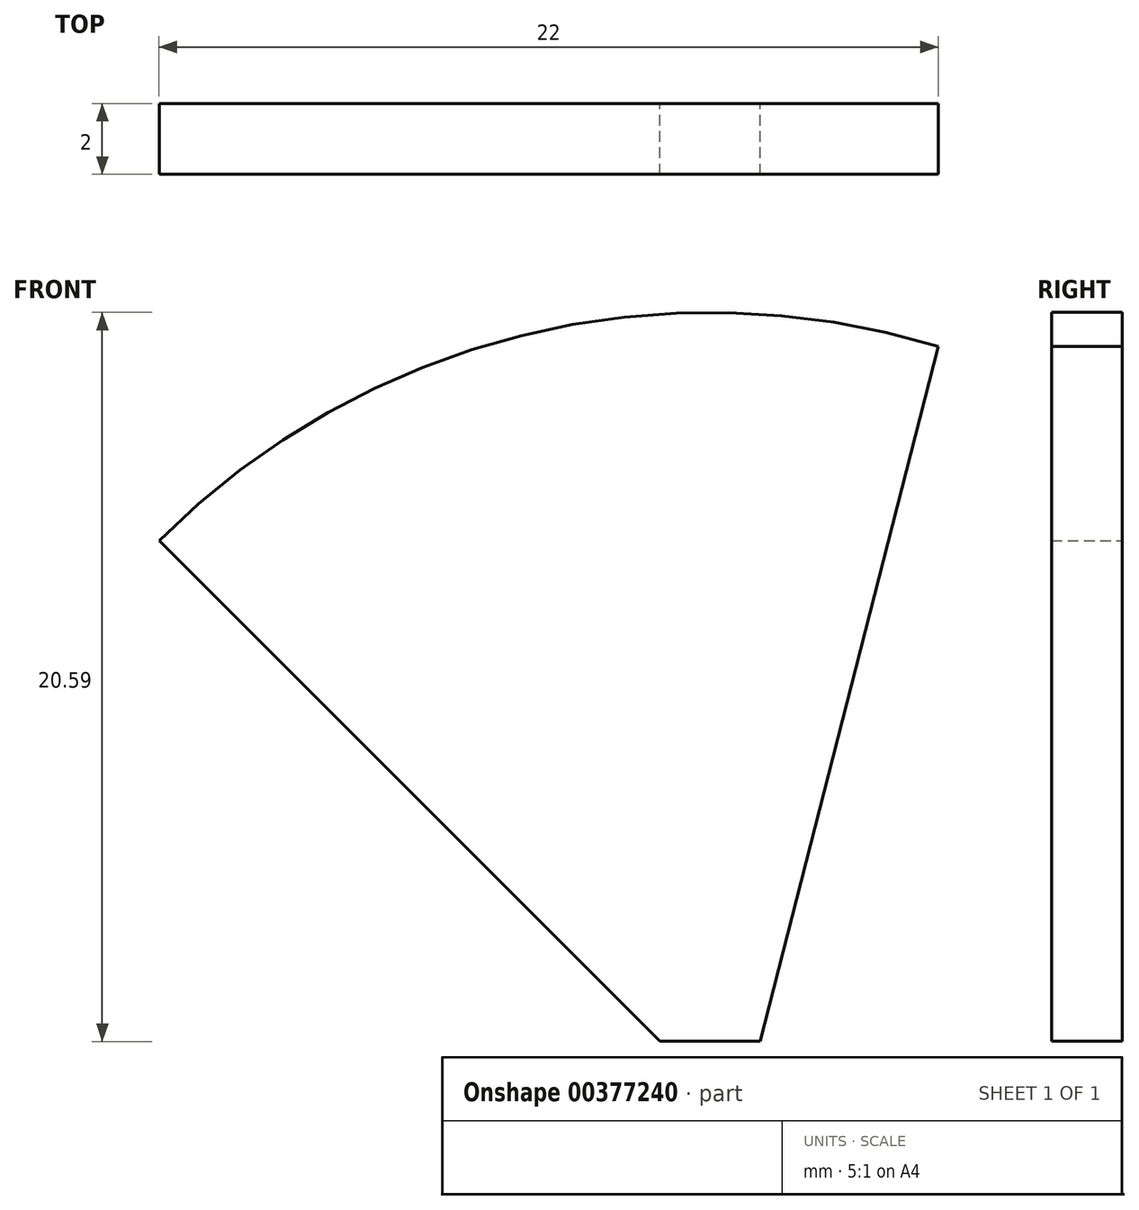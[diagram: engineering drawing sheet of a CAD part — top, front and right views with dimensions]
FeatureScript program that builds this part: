
annotation { "Feature Type Name" : "Feature", "Feature Type Description" : "" }
export const myFeature = defineFeature(function(context is Context, id is Id, definition is map)
    precondition{}
    {
        {
            var Q0;
            Q0=qCreatedBy(makeId("Front.planeOp"),FACE);
            var sketch = newSketch(context, id + "F0", { "sketchPlane" : qUnion([Q0])});
            skArc(sketch, "E0", {"start": v(6.44, 21.04) * mm, "mid": v(-5.32, 21.35) * mm, "end": v(-15.56, 15.56) * mm});
            skLineSegment(sketch, "E1", {"start": v(0, 0) * mm, "end": v(6.44, 21.04) * mm, "construction": true});
            skLineSegment(sketch, "E2", {"start": v(-15.56, 15.56) * mm, "end": v(-1.41, 1.41) * mm});
            skLineSegment(sketch, "E3", {"start": v(-15.56, 15.56) * mm, "end": v(6.44, 21.04) * mm, "construction": true});
            skLineSegment(sketch, "E4", {"start": v(-1.41, 1.41) * mm, "end": v(1.41, 1.41) * mm});
            skLineSegment(sketch, "E5", {"start": v(1.41, 1.41) * mm, "end": v(6.44, 21.04) * mm});
            skSolve(sketch);
        }
        {
            var Q0;
            Q0=makeQuery(id+"F0.imprint","IMPRINT",FACE,{"disambiguationData":[TD([[makeQuery(id+"F0.imprint","IMPRINT",EDGE,{"derivedFrom":sQuery(id+"F0.wireOp",EDGE,"E0")}),1.0]])]});
            extrude(context, id + "F1", {"entities" : qUnion([Q0]), "depth" : 2 * mm, "offsetDistance" : 25 * mm});
        }
    });
